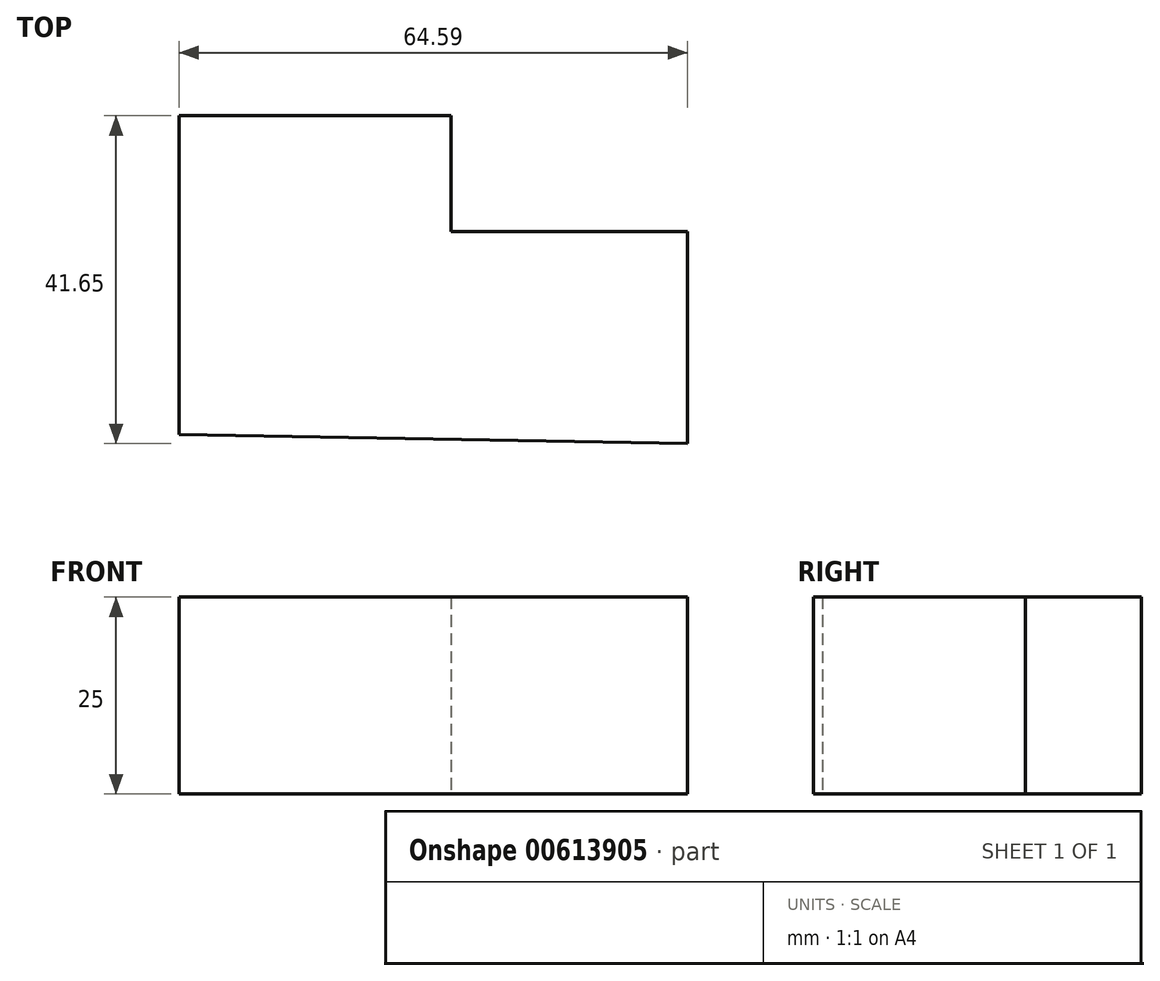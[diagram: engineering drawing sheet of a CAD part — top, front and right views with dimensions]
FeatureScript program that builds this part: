
annotation { "Feature Type Name" : "Feature", "Feature Type Description" : "" }
export const myFeature = defineFeature(function(context is Context, id is Id, definition is map)
    precondition{}
    {
        {
            var Q0;
            Q0=qCreatedBy(makeId("Top.planeOp"),FACE);
            var sketch = newSketch(context, id + "F0", { "sketchPlane" : qUnion([Q0])});
            skPoint(sketch, "E0.end.orphan", {"position": v(-54.81, 0) * mm});
            skLineSegment(sketch, "E1", {"start": v(-44.62, 28.19) * mm, "end": v(-44.62, -12.32) * mm});
            skLineSegment(sketch, "E2", {"start": v(-44.62, 28.19) * mm, "end": v(-10.06, 28.19) * mm});
            skLineSegment(sketch, "E3", {"start": v(-10.06, 28.19) * mm, "end": v(-10.06, 13.46) * mm});
            skLineSegment(sketch, "E4", {"start": v(-10.06, 13.46) * mm, "end": v(19.97, 13.46) * mm});
            skLineSegment(sketch, "E5", {"start": v(19.97, 13.46) * mm, "end": v(19.97, -13.46) * mm});
            skLineSegment(sketch, "E6", {"start": v(19.97, -13.46) * mm, "end": v(-44.62, -12.32) * mm});
            skSolve(sketch);
        }
        {
            var Q0;
            Q0 = qSketchRegion(id + "F0", true);
            extrude(context, id + "F1", {"entities" : qUnion([Q0]), "depth" : 25 * mm, "offsetDistance" : 25 * mm});
        }
    });
